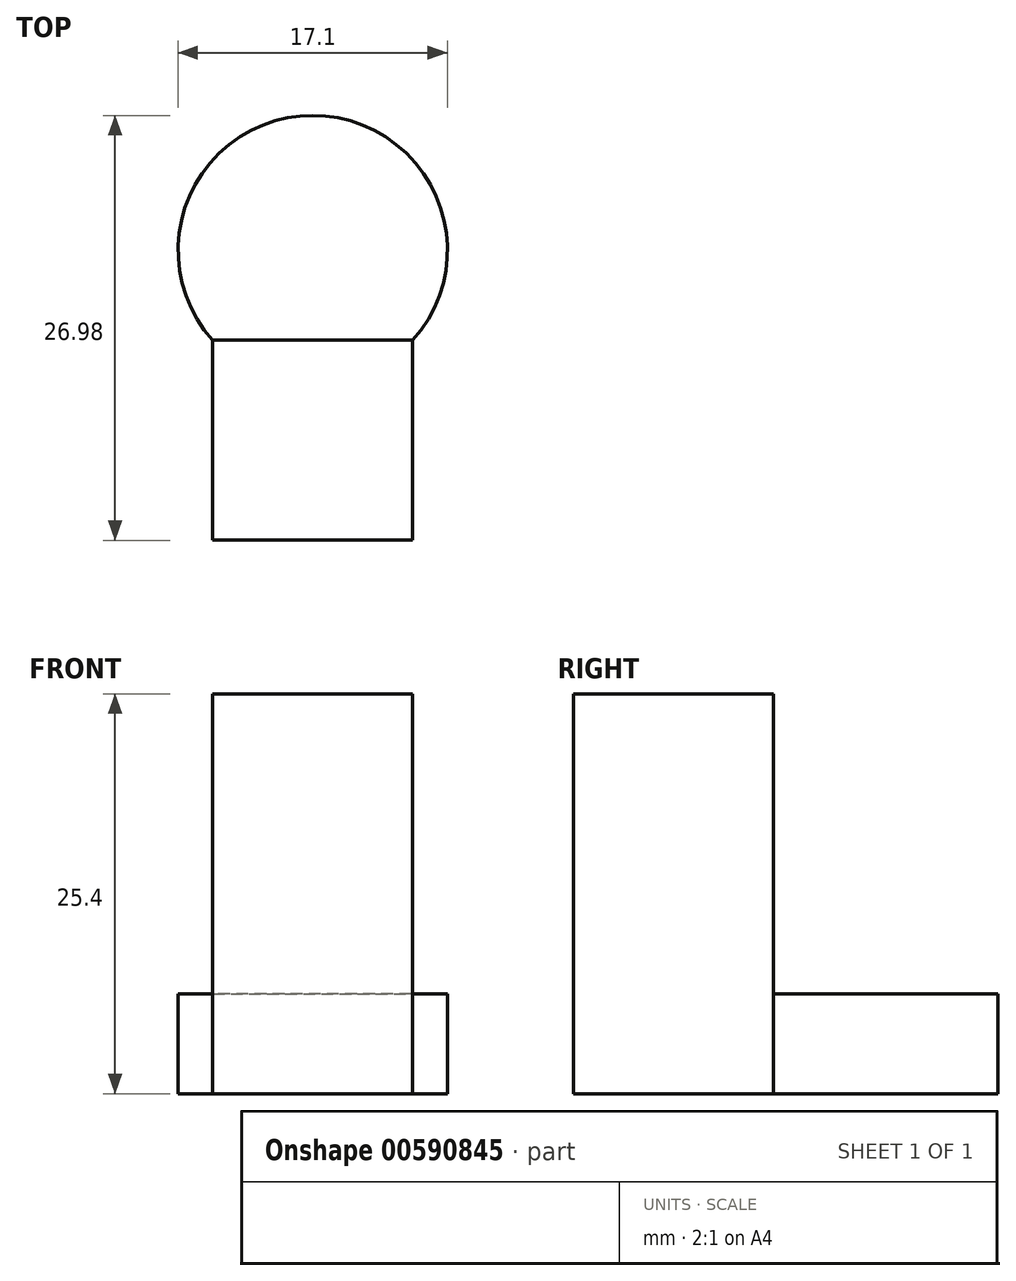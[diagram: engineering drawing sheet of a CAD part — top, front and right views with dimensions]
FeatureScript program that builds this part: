
annotation { "Feature Type Name" : "Feature", "Feature Type Description" : "" }
export const myFeature = defineFeature(function(context is Context, id is Id, definition is map)
    precondition{}
    {
        {
            var Q0;
            Q0=qCreatedBy(makeId("Top.planeOp"),FACE);
            var sketch = newSketch(context, id + "F0", { "sketchPlane" : qUnion([Q0])});
            skLineSegment(sketch, "E0", {"start": v(-22.18, 24.16) * mm, "end": v(-22.18, 11.46) * mm});
            skLineSegment(sketch, "E1", {"start": v(-22.18, 11.46) * mm, "end": v(-9.48, 11.46) * mm});
            skLineSegment(sketch, "E2", {"start": v(-9.48, 11.46) * mm, "end": v(-9.48, 24.16) * mm});
            skArc(sketch, "E3", {"start": v(-9.48, 24.16) * mm, "mid": v(-15.83, 38.44) * mm, "end": v(-22.18, 24.16) * mm});
            skLineSegment(sketch, "E4", {"start": v(-22.18, 24.16) * mm, "end": v(-9.48, 24.16) * mm});
            skSolve(sketch);
        }
        {
            var Q0;
            Q0=makeQuery(id+"F0.imprint","IMPRINT",FACE,{"disambiguationData":[TD([[makeQuery(id+"F0.imprint","IMPRINT",EDGE,{"derivedFrom":sQuery(id+"F0.wireOp",EDGE,"E0")}),1.0]])]});
            extrude(context, id + "F1", {"entities" : qUnion([Q0]), "depth" : 25.4 * mm, "offsetDistance" : 25.4 * mm});
        }
        {
            var Q0;
            Q0 = qSketchRegion(id + "F0", true);
            extrude(context, id + "F2", {"entities" : qUnion([Q0]), "operationType" : NewBodyOperationType.ADD, "depth" : 6.35 * mm, "offsetDistance" : 25.4 * mm});
        }
    });
